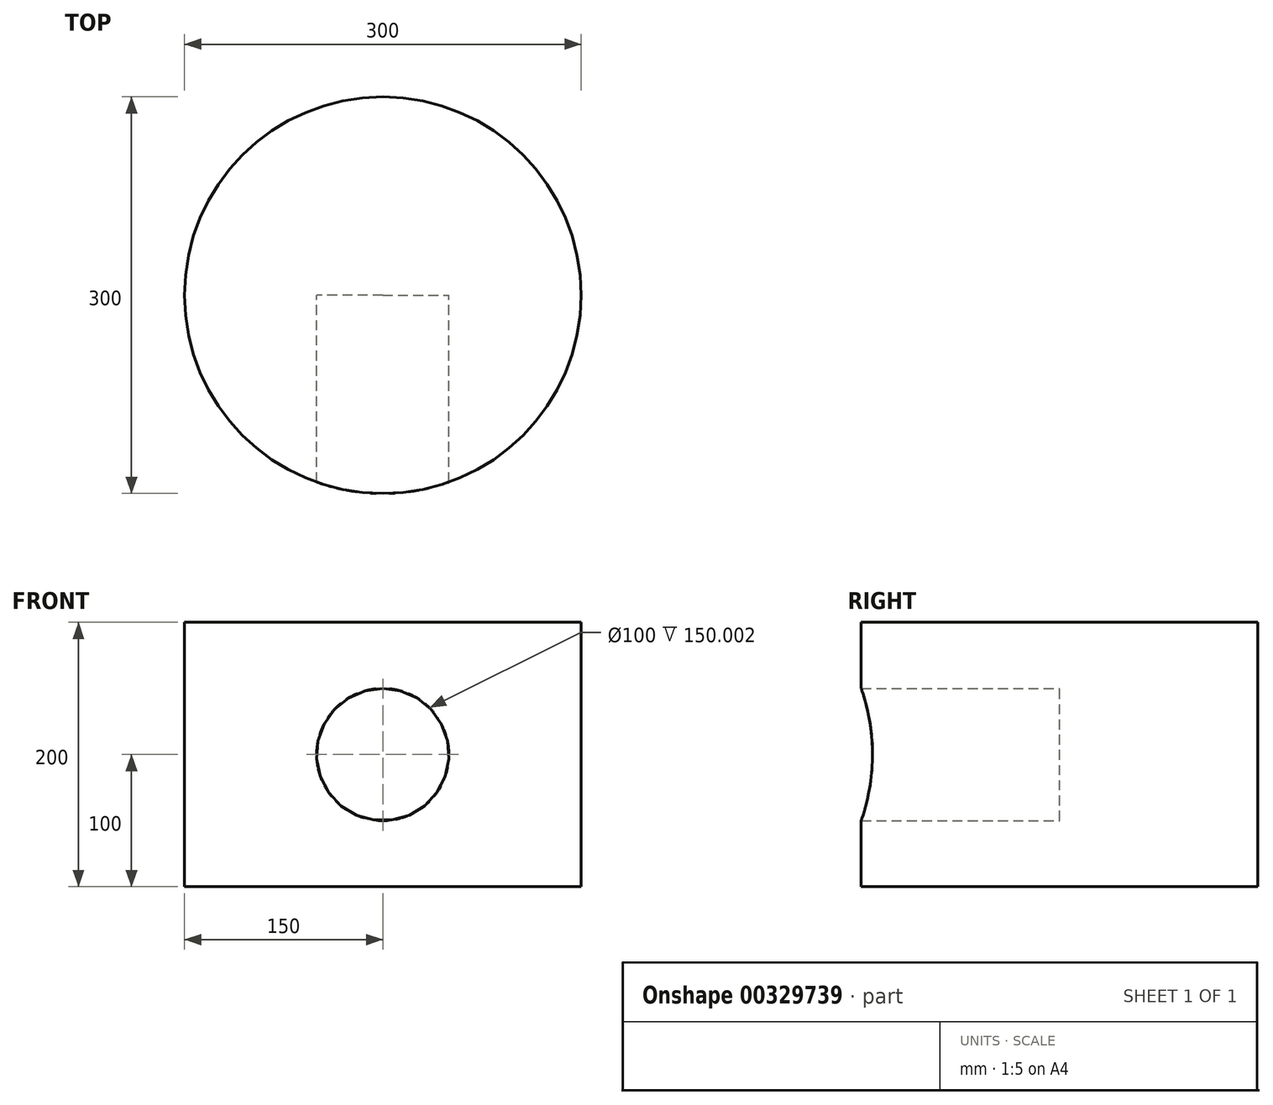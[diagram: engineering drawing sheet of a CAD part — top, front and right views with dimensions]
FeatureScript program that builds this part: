
annotation { "Feature Type Name" : "Feature", "Feature Type Description" : "" }
export const myFeature = defineFeature(function(context is Context, id is Id, definition is map)
    precondition{}
    {
        {
            var Q0;
            Q0=qCreatedBy(makeId("Top.planeOp"),FACE);
            var sketch = newSketch(context, id + "F0", { "sketchPlane" : qUnion([Q0])});
            skCircle(sketch, "E0", {"center": v(0, 0) * mm, "radius": 150 * mm});
            skSolve(sketch);
        }
        {
            var Q0;
            Q0=makeQuery(id+"F0.imprint","IMPRINT",FACE,{"disambiguationData":[TD([[makeQuery(id+"F0.imprint","IMPRINT",EDGE,{"derivedFrom":sQuery(id+"F0.wireOp",EDGE,"E0")}),1.0]])]});
            extrude(context, id + "F1", {"entities" : qUnion([Q0]), "endBound" : BoundingType.SYMMETRIC, "depth" : 200 * mm});
        }
        {
            var Q0;
            Q0=qCreatedBy(makeId("Front.planeOp"),FACE);
            var sketch = newSketch(context, id + "F2", { "sketchPlane" : qUnion([Q0])});
            skCircle(sketch, "E1", {"center": v(0, 0) * mm, "radius": 50 * mm});
            skSolve(sketch);
        }
        {
            var Q0;
            Q0 = qSketchRegion(id + "F2", true);
            extrude(context, id + "F3", {"entities" : qUnion([Q0]), "operationType" : NewBodyOperationType.REMOVE, "endBound" : BoundingType.UP_TO_NEXT, "depth" : 25 * mm});
        }
    });
